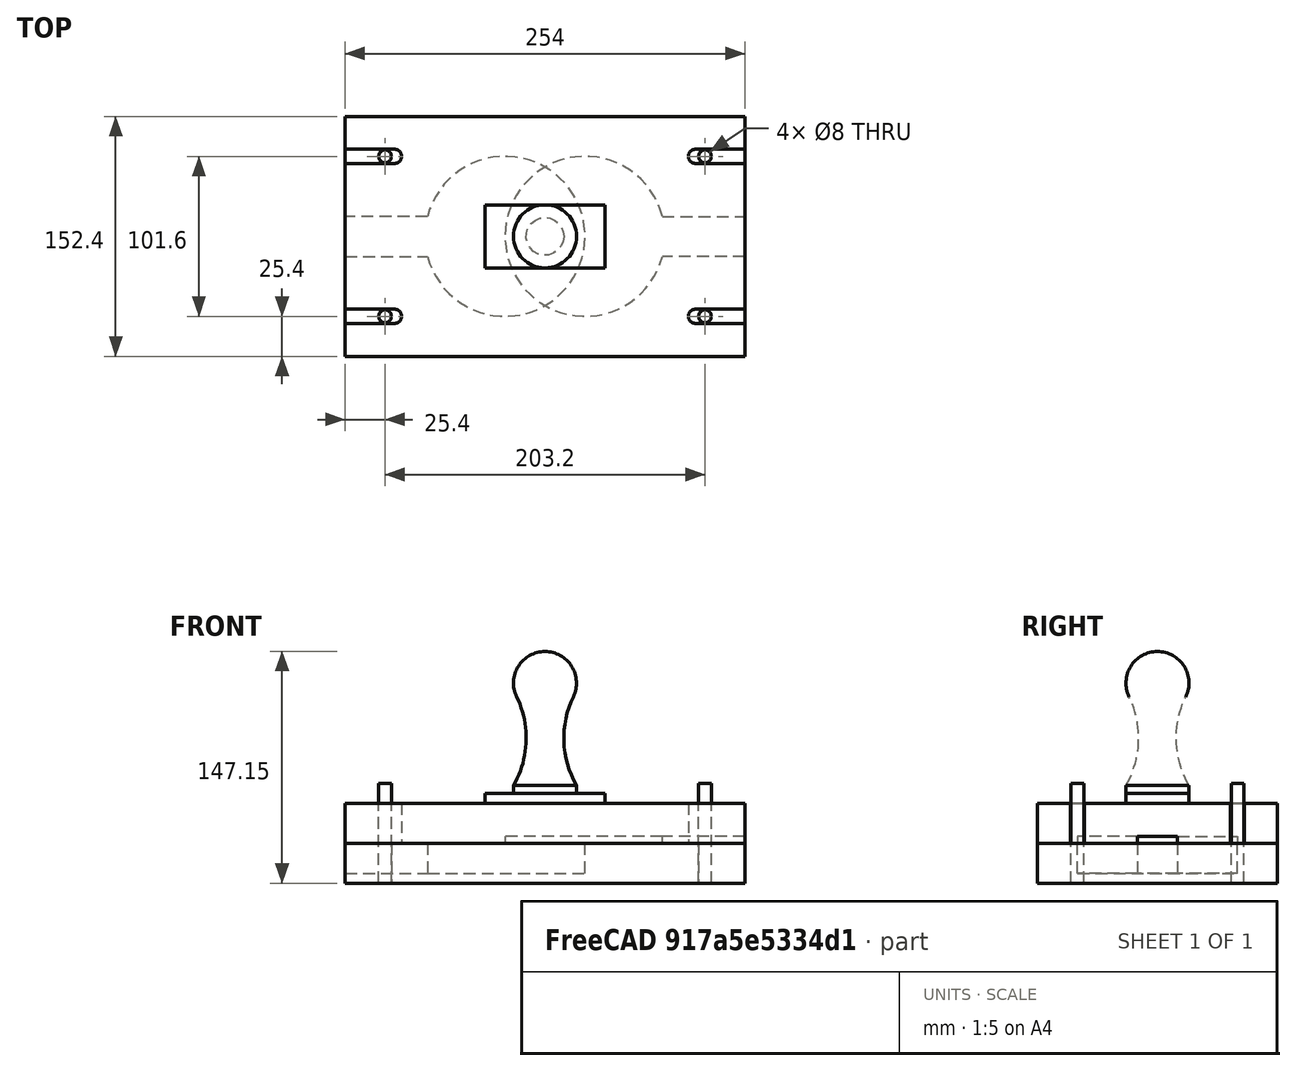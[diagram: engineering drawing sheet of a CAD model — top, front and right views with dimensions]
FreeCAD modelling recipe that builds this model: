
FCSTD DOCUMENT  (FreeCAD 0.17R13541 (Git))
Label: 贝尔的金属探测器 FEM
License: All rights reserved
LicenseURL: http://en.wikipedia.org/wiki/All_rights_reserved
objects: Sketcher::SketchObject×8, PartDesign::Pocket×4, Part::Cylinder×4, PartDesign::Mirrored×4, PartDesign::Pad×3, PartDesign::Body×3, PartDesign::MultiTransform×2, PartDesign::ShapeBinder×2, Fem::FemSolverObjectPython×2, Part::Feature×2, Fem::FemMeshObjectPython×2, Fem::ConstraintFixed×2, Fem::ConstraintForce×2, App::MaterialObjectPython×2, PartDesign::Revolution×1, Part::Compound×1, Part::Fuse×1, Fem::FemAnalysis×1
note: 43 computed .brp shape members not serialized (recipe doc carries the construction recipe); baked Part::Feature solids carry a one-line shape summary decoded from their .brp

FEATURE [Sketcher::SketchObject] Sketch
  MapMode = 5
  Support = -> [XY_Plane]
  sketch-geometry (4):
    g0: LineSegment StartX=127 StartY=76.2 StartZ=0 EndX=-127 EndY=76.2 EndZ=0
    g1: LineSegment StartX=-127 StartY=76.2 StartZ=0 EndX=-127 EndY=-76.2 EndZ=0
    g2: LineSegment StartX=-127 StartY=-76.2 StartZ=0 EndX=127 EndY=-76.2 EndZ=0
    g3: LineSegment StartX=127 StartY=-76.2 StartZ=0 EndX=127 EndY=76.2 EndZ=0
  constraints (11):
    c: Coincident(g0,g1)
    c: Coincident(g1,g2)
    c: Coincident(g2,g3)
    c: Coincident(g3,g0)
    c: Horizontal(g0)
    c: Horizontal(g2)
    c: Vertical(g1)
    c: Vertical(g3)
    c: DistanceX(g0,g0) = 254
    c: DistanceY(g2,g0) = 152.4
    c: Symmetric(g0,g1,g-1)
FEATURE [PartDesign::Pad] Pad  label="上基座"
  Length = 25.4
  Length2 = 100
  Profile = -> Sketch
  Type = 0
FEATURE [Sketcher::SketchObject] Sketch001
  MapMode = 5
  Placement = pos=(0,0,25.4) rot=(0,0,1;0rad)
  Support = -> [Pad]
  sketch-geometry (1):
    g0: Circle CenterX=-101.6 CenterY=50.8 CenterZ=0 NormalX=0 NormalY=0 NormalZ=1 AngleXU=0 Radius=4
  constraints (3):
    c: DistanceX(g0) = -101.6
    c: DistanceY(g0) = 50.8
    c: Radius(g0) = 4
FEATURE [PartDesign::Pocket] Pocket  label="销钉孔"
  BaseFeature = -> Pad
  Length = 5
  Length2 = 100
  Profile = -> Sketch001
  Type = 1
FEATURE [Part::Cylinder] Cylinder  label="销钉1"
  Angle = 360
  AttacherType = Attacher::AttachEngine3D
  Height = 63.5
  Placement = pos=(-101.6,50.8,0) rot=(0,0,1;0rad)
  Radius = 4
FEATURE [Part::Cylinder] Cylinder001  label="销钉2"
  Angle = 360
  AttacherType = Attacher::AttachEngine3D
  Height = 63.5
  Placement = pos=(101.6,50.8,0) rot=(0,0,1;0rad)
  Radius = 4
FEATURE [Part::Cylinder] Cylinder002  label="销钉3"
  Angle = 360
  AttacherType = Attacher::AttachEngine3D
  Height = 63.5
  Placement = pos=(-101.6,-50.8,0) rot=(0,0,1;0rad)
  Radius = 4
FEATURE [Part::Cylinder] Cylinder003  label="销钉4"
  Angle = 360
  AttacherType = Attacher::AttachEngine3D
  Height = 63.5
  Placement = pos=(101.6,-50.8,0) rot=(0,0,1;0rad)
  Radius = 4
FEATURE [PartDesign::Mirrored] Mirrored
  MirrorPlane = -> YZ_Plane
FEATURE [PartDesign::Mirrored] Mirrored001
  MirrorPlane = -> XZ_Plane
FEATURE [PartDesign::MultiTransform] MultiTransform  label="两次镜像的销钉孔"
  BaseFeature = -> Pocket
  Originals = -> [Pocket]
  Transformations = -> [Mirrored,Mirrored001]
FEATURE [Sketcher::SketchObject] Sketch002
  ExternalGeometry = -> [MultiTransform]
  MapMode = 5
  Placement = pos=(0,0,25.4) rot=(0,0,1;0rad)
  Support = -> [MultiTransform]
  sketch-geometry (4):
    g0: LineSegment StartX=-127 StartY=-12.7 StartZ=0 EndX=-74.5869 EndY=-12.7 EndZ=0
    g1: LineSegment StartX=-74.5869 StartY=12.7 StartZ=0 EndX=-127 EndY=12.7 EndZ=0
    g2: LineSegment StartX=-127 StartY=12.7 StartZ=0 EndX=-127 EndY=-12.7 EndZ=0
    g3: ArcOfCircle CenterX=-25.4 CenterY=0 CenterZ=0 NormalX=0 NormalY=0 NormalZ=1 AngleXU=0 Radius=50.8 StartAngle=3.39427 EndAngle=9.1721
  constraints (13):
    c: Coincident(g1,g2)
    c: Coincident(g2,g0)
    c: Horizontal(g0)
    c: Horizontal(g1)
    c: Vertical(g2)
    c: PointOnObject(g0,g-3)
    c: PointOnObject(g3,g-1)  '凹坑中心在x轴上'
    c: Symmetric(g1,g0,g-1)  '沟槽中心对称'
    c: DistanceY(g0,g1) = 25.4  '沟槽宽度'
    c: Radius(g3) = 50.8  '凹坑半径'
    c: DistanceX(g3,g-1) = 25.4  '凹坑位置'
    c: Coincident(g3,g0)
    c: Coincident(g3,g1)
FEATURE [PartDesign::Pocket] Pocket001  label="深沟槽和凹坑"
  BaseFeature = -> MultiTransform
  Length = 19.05
  Length2 = 100
  Profile = -> Sketch002
  Type = 0
FEATURE [PartDesign::Body] Body  label="下底座"
  Group = -> [Sketch,Pad,Sketch001,Pocket,MultiTransform,Mirrored,Mirrored001,Sketch002,Pocket001]
  Origin = -> Origin
  Tip = -> Pocket001
FEATURE [PartDesign::ShapeBinder] ShapeBinder  label="引用的下底座的顶面"
  Support = -> [Pocket001]
FEATURE [Sketcher::SketchObject] Sketch003
  ExternalGeometry = -> [ShapeBinder]
  MapMode = 5
  Placement = pos=(0,0,25.4) rot=(0,0,1;0rad)
  Support = -> [ShapeBinder]
  sketch-geometry (4):
    g0: LineSegment StartX=-127 StartY=76.2 StartZ=0 EndX=127 EndY=76.2 EndZ=0
    g1: LineSegment StartX=127 StartY=76.2 StartZ=0 EndX=127 EndY=-76.2 EndZ=0
    g2: LineSegment StartX=127 StartY=-76.2 StartZ=0 EndX=-127 EndY=-76.2 EndZ=0
    g3: LineSegment StartX=-127 StartY=-76.2 StartZ=0 EndX=-127 EndY=76.2 EndZ=0
  constraints (10):
    c: Coincident(g0,g1)
    c: Coincident(g1,g2)
    c: Coincident(g2,g3)
    c: Coincident(g3,g0)
    c: Horizontal(g0)
    c: Horizontal(g2)
    c: Vertical(g1)
    c: Vertical(g3)
    c: Coincident(g0,g-3)
    c: Coincident(g1,g-4)
FEATURE [PartDesign::Pad] Pad001  label="下基座"
  Length = 25.4
  Length2 = 100
  Profile = -> Sketch003
  Type = 0
FEATURE [Sketcher::SketchObject] Sketch004
  ExternalGeometry = -> [ShapeBinder]
  MapMode = 5
  Placement = pos=(0,0,25.4) rot=(0,0,1;0rad)
  Support = -> [ShapeBinder]
  sketch-geometry (5):
    g0: LineSegment [constr] StartX=-101.6 StartY=50.8 StartZ=0 EndX=-95.6 EndY=50.8 EndZ=0
    g1: ArcOfCircle CenterX=-95.6 CenterY=50.8 CenterZ=0 NormalX=0 NormalY=0 NormalZ=1 AngleXU=0 Radius=4.5 StartAngle=4.71239 EndAngle=7.85398
    g2: LineSegment StartX=-95.6 StartY=55.3 StartZ=0 EndX=-127 EndY=55.3 EndZ=0
    g3: LineSegment StartX=-127 StartY=55.3 StartZ=0 EndX=-127 EndY=46.3 EndZ=0
    g4: LineSegment StartX=-127 StartY=46.3 StartZ=0 EndX=-95.6 EndY=46.3 EndZ=0
  constraints (13):
    c: Coincident(g0,g-3)
    c: Horizontal(g0)
    c: Coincident(g1,g0)
    c: PointOnObject(g2,g-4)
    c: Horizontal(g2)
    c: Coincident(g3,g2)
    c: Coincident(g4,g3)
    c: Horizontal(g4)
    c: Tangent(g4,g1) = -1.5708
    c: Tangent(g2,g1) = -1.5708
    c: DistanceX(g0,g0) = 6
    c: Radius(g1) = 4.5
    c: Vertical(g3)
FEATURE [PartDesign::Pocket] Pocket002  label="滑槽"
  BaseFeature = -> Pad001
  Length = 5
  Length2 = 100
  Profile = -> Sketch004
  Reversed = true
  Type = 1
FEATURE [Sketcher::SketchObject] Sketch005
  ExternalGeometry = -> [ShapeBinder]
  MapMode = 5
  Placement = pos=(0,0,25.4) rot=(0,0,1;0rad)
  Support = -> [ShapeBinder]
  sketch-geometry (5):
    g0: LineSegment [constr] StartX=-74.5869 StartY=12.7 StartZ=0 EndX=-74.5869 EndY=-12.7 EndZ=0
    g1: LineSegment StartX=127 StartY=-12.7 StartZ=0 EndX=74.5869 EndY=-12.7 EndZ=0
    g2: LineSegment StartX=74.5869 StartY=12.7 StartZ=0 EndX=127 EndY=12.7 EndZ=0
    g3: LineSegment StartX=127 StartY=12.7 StartZ=0 EndX=127 EndY=-12.7 EndZ=0
    g4: ArcOfCircle CenterX=25.4 CenterY=0 CenterZ=0 NormalX=0 NormalY=0 NormalZ=1 AngleXU=0 Radius=50.8 StartAngle=0.25268 EndAngle=6.03051
  constraints (15):
    c: Coincident(g0,g-3)
    c: Coincident(g0,g-3)
    c: Coincident(g2,g3)
    c: Coincident(g3,g1)
    c: Horizontal(g1)
    c: Horizontal(g2)
    c: Vertical(g3)
    c: PointOnObject(g1,g-4)
    c: PointOnObject(g4,g-1)
    c: Symmetric(g2,g1,g-1)  '沟槽沿x轴对称'
    c: Equal(g3,g0)  '沟槽宽度相等'
    c: Equal(g4,g-3)  '两圆大小相等'
    c: Coincident(g4,g2)
    c: Coincident(g4,g1)
    c: Symmetric(g4,g-3,g-1)  '两圆镜像'
FEATURE [PartDesign::Pocket] Pocket003  label="浅沟槽和凹坑"
  BaseFeature = -> Pocket002
  Length = 4.318
  Length2 = 100
  Profile = -> Sketch005
  Reversed = true
  Type = 0
FEATURE [PartDesign::Mirrored] Mirrored002
  MirrorPlane = -> YZ_Plane001
FEATURE [PartDesign::Mirrored] Mirrored003
  MirrorPlane = -> XZ_Plane001
FEATURE [PartDesign::MultiTransform] MultiTransform001  label="两次镜像的滑槽"
  BaseFeature = -> Pocket003
  Originals = -> [Pocket002]
  Transformations = -> [Mirrored002,Mirrored003]
FEATURE [PartDesign::Body] Body001  label="上部块"
  Group = -> [ShapeBinder,Sketch003,Pad001,Sketch004,Pocket002,Sketch005,Pocket003,MultiTransform001,Mirrored002,Mirrored003]
  Origin = -> Origin001
  Tip = -> MultiTransform001
FEATURE [PartDesign::ShapeBinder] ShapeBinder001  label="引用的上部块的顶面"
  Support = -> [MultiTransform001]
FEATURE [Sketcher::SketchObject] Sketch006
  MapMode = 5
  Placement = pos=(0,0,50.8) rot=(0,0,1;0rad)
  Support = -> [ShapeBinder001]
  sketch-geometry (4):
    g0: LineSegment StartX=38.1 StartY=20 StartZ=0 EndX=-38.1 EndY=20 EndZ=0
    g1: LineSegment StartX=-38.1 StartY=20 StartZ=0 EndX=-38.1 EndY=-20 EndZ=0
    g2: LineSegment StartX=-38.1 StartY=-20 StartZ=0 EndX=38.1 EndY=-20 EndZ=0
    g3: LineSegment StartX=38.1 StartY=-20 StartZ=0 EndX=38.1 EndY=20 EndZ=0
  constraints (11):
    c: Coincident(g0,g1)
    c: Coincident(g1,g2)
    c: Coincident(g2,g3)
    c: Coincident(g3,g0)
    c: Horizontal(g0)
    c: Horizontal(g2)
    c: Vertical(g1)
    c: Vertical(g3)
    c: Symmetric(g0,g1,g-1)
    c: DistanceX(g0,g0) = 76.2
    c: DistanceY(g2,g0) = 40
FEATURE [PartDesign::Pad] Pad002  label="手柄座"
  Length = 6.35
  Length2 = 100
  Profile = -> Sketch006
  Type = 0
FEATURE [Sketcher::SketchObject] Sketch007
  ExternalGeometry = -> [Pad002]
  MapMode = 5
  Placement = pos=(0,0,0) rot=(1,0,0;1.5708rad)
  Support = -> [XZ_Plane002]
  sketch-geometry (5):
    g0: LineSegment StartX=0 StartY=57.15 StartZ=0 EndX=20 EndY=57.15 EndZ=0
    g1: LineSegment StartX=20 StartY=57.15 StartZ=0 EndX=20 EndY=62.15 EndZ=0
    g2: ArcOfCircle CenterX=71.9485 CenterY=92.1726 CenterZ=0 NormalX=0 NormalY=0 NormalZ=1 AngleXU=0 Radius=60 StartAngle=2.68909 EndAngle=3.66563
    g3: ArcOfCircle CenterX=0 CenterY=127.15 CenterZ=0 NormalX=0 NormalY=0 NormalZ=1 AngleXU=0 Radius=20 StartAngle=5.83068 EndAngle=7.85398
    g4: LineSegment StartX=0 StartY=147.15 StartZ=0 EndX=0 EndY=57.15 EndZ=0
  constraints (16):
    c: PointOnObject(g0,g-3)
    c: PointOnObject(g0,g-3)
    c: Coincident(g0,g1)
    c: Vertical(g1)
    c: Coincident(g2,g1)
    c: Coincident(g4,g3)
    c: Coincident(g4,g0)
    c: Vertical(g4)
    c: Perpendicular(g3,g4)
    c: PointOnObject(g4,g-2)
    c: Tangent(g3,g2) = 1.5708
    c: DistanceX(g0,g0) = 20
    c: DistanceY(g0,g1) = 5
    c: Radius(g2) = 60
    c: DistanceY(g0,g3) = 90
    c: DistanceY(g0,g3) = 70
FEATURE [PartDesign::Revolution] Revolution  label="把手"
  Angle = 360
  Axis = (0,0,1)
  Base = (0,0,0)
  BaseFeature = -> Pad002
  Profile = -> Sketch007
  ReferenceAxis = -> Sketch007 [V_Axis]
  Reversed = true
FEATURE [PartDesign::Body] Body002  label="手柄"
  Group = -> [ShapeBinder001,Sketch006,Pad002,Sketch007,Revolution]
  Origin = -> Origin002
  Tip = -> Revolution
FEATURE [Part::Compound] Compound  label="四个销钉"
  Links = -> [Cylinder,Cylinder001,Cylinder003,Cylinder002]
FEATURE [Fem::FemSolverObjectPython] CalculiXccxTools  # FEM object (typed FeaturePython)
  AnalysisType = 0
  BeamShellResultOutput3D = false
  EigenmodeHighLimit = 1000000
  EigenmodeLowLimit = 0
  EigenmodesCount = 10
  GeometricalNonlinearity = 0
  IterationsControlParameterCutb = 0.25,0.5,0.75,0.85,,,1.5,
  IterationsControlParameterIter = 4,8,9,200,10,400,,200,,
  IterationsControlParameterTimeUse = false
  IterationsThermoMechMaximum = 2000
  IterationsUserDefinedIncrementations = false
  IterationsUserDefinedTimeStepLength = false
  MaterialNonlinearity = 0
  MatrixSolverType = 0
  SplitInputWriter = false
  ThermoMechSteadyState = true
  TimeEnd = 1
  TimeInitialStep = 0.01
FEATURE [Part::Feature] Body001001  label="上部块001"
  shape: bbox 254 x 152.4 x 25.4 mm, 26 faces (baked)
FEATURE [Part::Feature] Body002001  label="手柄001"
  shape: bbox 76.2 x 63.53 x 97.58 mm, 10 faces (baked)
FEATURE [Part::Fuse] Fusion  label="用于FEM的模型"
  Base = -> Body001001
  Tool = -> Body002001
FEATURE [Fem::FemMeshObjectPython] FEMMeshGmsh  # FEM object (typed FeaturePython)
  Algorithm2D = 0
  Algorithm3D = 0
  CharacteristicLengthMax = 0
  CharacteristicLengthMin = 0
  CoherenceMesh = true
  ElementDimension = 0
  ElementOrder = 1
  GeometryTolerance = 1e-06
  GroupsOfNodes = false
  HighOrderOptimize = false
  OptimizeNetgen = false
  OptimizeStd = true
  Part = -> Fusion
  RecombineAll = false
FEATURE [Fem::ConstraintFixed] FemConstraintFixed
  NormalDirection = (0,0,-1)
  Normals = (14) [(0,0,-1),(0,0,-1),(0,0,-1),(0,0,-1),(0,0,-1),(0,0,-1),(0,0,-1),(0,0,-1),(0,0,-1),(0,0,-1),(0,0,-1),(0,0,-1),(0,0,-1),(0,0,-1)]
  Points = (14) [(127,-76.2,25.4),(42.3333,-76.2,25.4),(-42.3333,-76.2,25.4),(-127,-76.2,25.4),(127,-25.4,25.4),(-42.3333,-25.4,25.4),(-127,-25.4,25.4),+7 more]
  References = -> [Fusion]
  Scale = 15
FEATURE [Fem::ConstraintForce] FemConstraintForce
  DirectionVector = (1,0,0)
  Force = 1
  NormalDirection = (-1,0,0)
  Points = (56) [(-38.1,20,57.15),(-38.1,6.66667,57.15),(-38.1,-6.66667,57.15),(-38.1,-20,57.15),(-38.1,20,53.975),(-38.1,6.66667,53.975),(-38.1,-6.66667,53.975),+49 more]
  References = -> [Fusion]
  Reversed = true
  Scale = 6
FEATURE [App::MaterialObjectPython] SolidMaterial  # material (typed FeaturePython)
  Category = 0
  Material = Density=700.0 kg/m^3,Description=A standard construction wood,Father=Aggregate,Name=Wood,PoissonRatio=0.05,+5 more (map truncated)
FEATURE [Fem::FemSolverObjectPython] CalculiXccxTools001  # FEM object (typed FeaturePython)
  AnalysisType = 0
  BeamShellResultOutput3D = false
  EigenmodeHighLimit = 1000000
  EigenmodeLowLimit = 0
  EigenmodesCount = 10
  GeometricalNonlinearity = 0
  IterationsControlParameterCutb = 0.25,0.5,0.75,0.85,,,1.5,
  IterationsControlParameterIter = 4,8,9,200,10,400,,200,,
  IterationsControlParameterTimeUse = false
  IterationsThermoMechMaximum = 2000
  IterationsUserDefinedIncrementations = false
  IterationsUserDefinedTimeStepLength = false
  MaterialNonlinearity = 0
  MatrixSolverType = 0
  SplitInputWriter = false
  ThermoMechSteadyState = true
  TimeEnd = 1
  TimeInitialStep = 0.01
FEATURE [Fem::FemMeshObjectPython] FEMMeshGmsh001  # FEM object (typed FeaturePython)
  Algorithm2D = 0
  Algorithm3D = 0
  CharacteristicLengthMax = 0
  CharacteristicLengthMin = 0
  CoherenceMesh = true
  ElementDimension = 0
  ElementOrder = 1
  GeometryTolerance = 1e-06
  GroupsOfNodes = false
  HighOrderOptimize = false
  OptimizeNetgen = false
  OptimizeStd = true
  Part = -> Fusion
  RecombineAll = false
FEATURE [Fem::ConstraintFixed] FemConstraintFixed001
  NormalDirection = (0,0,-1)
  Normals = (14) [(0,0,-1),(0,0,-1),(0,0,-1),(0,0,-1),(0,0,-1),(0,0,-1),(0,0,-1),(0,0,-1),(0,0,-1),(0,0,-1),(0,0,-1),(0,0,-1),(0,0,-1),(0,0,-1)]
  Points = (14) [(127,-76.2,25.4),(42.3333,-76.2,25.4),(-42.3333,-76.2,25.4),(-127,-76.2,25.4),(127,-25.4,25.4),(-42.3333,-25.4,25.4),(-127,-25.4,25.4),+7 more]
  References = -> [Fusion]
  Scale = 15
FEATURE [Fem::ConstraintForce] FemConstraintForce001
  DirectionVector = (1,0,0)
  Force = 9000
  NormalDirection = (-1,0,0)
  Points = (56) [(-38.1,20,57.15),(-38.1,6.66667,57.15),(-38.1,-6.66667,57.15),(-38.1,-20,57.15),(-38.1,20,53.975),(-38.1,6.66667,53.975),(-38.1,-6.66667,53.975),+49 more]
  References = -> [Fusion]
  Reversed = true
  Scale = 6
FEATURE [App::MaterialObjectPython] SolidMaterial001  # material (typed FeaturePython)
  Category = 0
  Material = Density=700.0 kg/m^3,Description=A standard construction wood,Father=Aggregate,Name=Wood,PoissonRatio=0.05,+5 more (map truncated)
FEATURE [Fem::FemAnalysis] Analysis001
  Group = -> [CalculiXccxTools001,FEMMeshGmsh001,FemConstraintFixed001,FemConstraintForce001,SolidMaterial001]
